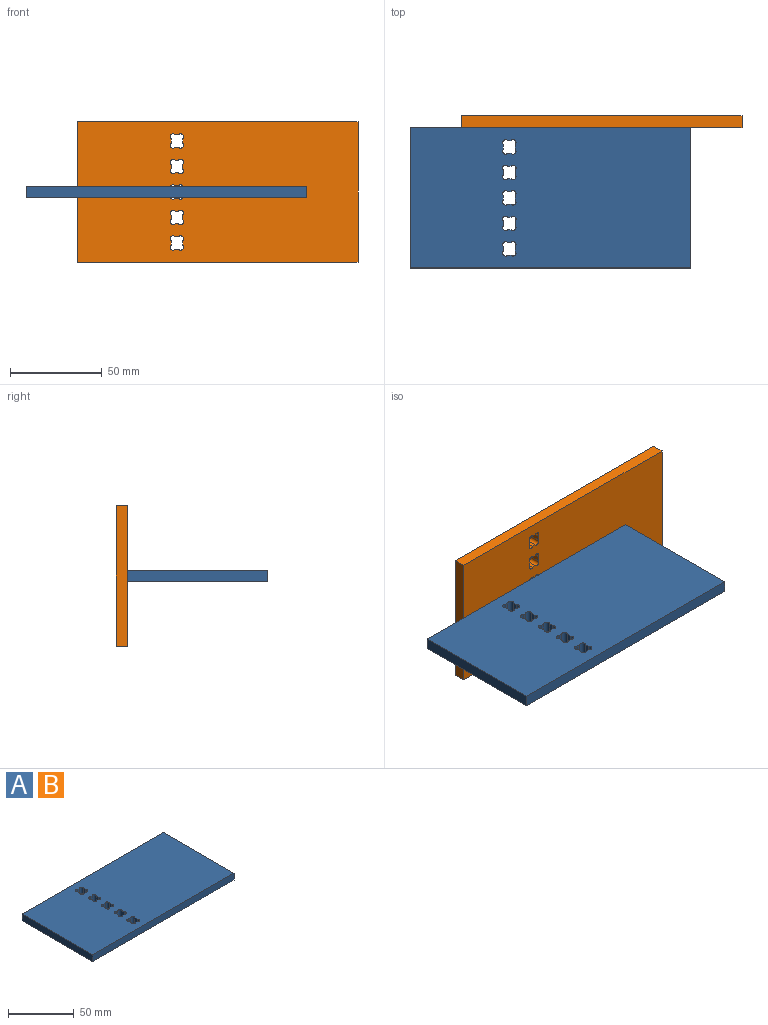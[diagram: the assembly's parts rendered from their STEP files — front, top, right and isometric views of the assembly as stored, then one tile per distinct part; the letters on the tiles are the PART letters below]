
ASSEMBLY  parts=2 mates=1
PART A: 46 faces, bbox 152.4x76.2x6.4 mm
  f0: plane 6.35x1.86mm, normal (0,-1,0), area 11.8mm2, adj f24,f25,f42,f45
  f1: plane 6.35x2.44mm, normal (-1,0,0), area 15.5mm2, adj f24,f25,f44,f45
  f2: plane 6.35x1.86mm, normal (0,1,0), area 11.8mm2, adj f24,f25,f43,f44
  f3: plane 6.35x2.44mm, normal (1,0,0), area 15.5mm2, adj f24,f25,f42,f43
  f4: plane 6.35x1.86mm, normal (0,-1,0), area 11.8mm2, adj f24,f25,f38,f41
  f5: plane 6.35x2.44mm, normal (-1,0,0), area 15.5mm2, adj f24,f25,f40,f41
  f6: plane 6.35x1.86mm, normal (0,1,0), area 11.8mm2, adj f24,f25,f39,f40
  f7: plane 6.35x2.44mm, normal (1,0,0), area 15.5mm2, adj f24,f25,f38,f39
  f8: plane 6.35x1.86mm, normal (0,-1,0), area 11.8mm2, adj f24,f25,f34,f37
  f9: plane 6.35x2.44mm, normal (-1,0,0), area 15.5mm2, adj f24,f25,f36,f37
  f10: plane 6.35x1.86mm, normal (0,1,0), area 11.8mm2, adj f24,f25,f35,f36
  f11: plane 6.35x2.44mm, normal (1,0,0), area 15.5mm2, adj f24,f25,f34,f35
  f12: plane 6.35x1.86mm, normal (0,-1,0), area 11.8mm2, adj f24,f25,f30,f33
  f13: plane 6.35x2.44mm, normal (-1,0,0), area 15.5mm2, adj f24,f25,f32,f33
  f14: plane 6.35x1.86mm, normal (0,1,0), area 11.8mm2, adj f24,f25,f31,f32
  f15: plane 6.35x2.44mm, normal (1,0,0), area 15.5mm2, adj f24,f25,f30,f31
  f16: plane 6.35x1.86mm, normal (0,-1,0), area 11.8mm2, adj f24,f25,f26,f29
  f17: plane 6.35x2.44mm, normal (-1,0,0), area 15.5mm2, adj f24,f25,f28,f29
  f18: plane 6.35x1.86mm, normal (0,1,0), area 11.8mm2, adj f24,f25,f27,f28
  f19: plane 6.35x2.44mm, normal (1,0,0), area 15.5mm2, adj f24,f25,f26,f27
  f20: plane 152.4x6.35mm, normal (0,1,0), area 967.7mm2, adj f21,f23,f24,f25
  f21: plane 76.2x6.35mm, normal (-1,0,0), area 483.9mm2, adj f20,f22,f24,f25
  f22: plane 152.4x6.35mm, normal (0,-1,0), area 967.7mm2, adj f21,f23,f24,f25
  f23: plane 76.2x6.35mm, normal (1,0,0), area 483.9mm2, adj f20,f22,f24,f25
  f24: plane 152.4x76.2mm, normal (0,0,1), area 11364.2mm2, adj f0,f1,f2,f3,f4,f5,f6,f7
  f25: plane 152.4x76.2mm, normal (0,0,-1), area 11364.2mm2, adj f0,f1,f2,f3,f4,f5,f6,f7
  f26: cylinder r=1.59mm len=6.35mm, axis (0,0,1), area 31.7mm2, adj f16,f19,f24,f25
  f27: cylinder r=1.59mm len=6.35mm, axis (0,0,1), area 31.7mm2, adj f18,f19,f24,f25
  f28: cylinder r=1.59mm len=6.35mm, axis (0,0,1), area 31.7mm2, adj f17,f18,f24,f25
  f29: cylinder r=1.59mm len=6.35mm, axis (0,0,1), area 31.7mm2, adj f16,f17,f24,f25
  f30: cylinder r=1.59mm len=6.35mm, axis (0,0,1), area 31.7mm2, adj f12,f15,f24,f25
  f31: cylinder r=1.59mm len=6.35mm, axis (0,0,1), area 31.7mm2, adj f14,f15,f24,f25
  f32: cylinder r=1.59mm len=6.35mm, axis (0,0,1), area 31.7mm2, adj f13,f14,f24,f25
  f33: cylinder r=1.59mm len=6.35mm, axis (0,0,1), area 31.7mm2, adj f12,f13,f24,f25
  f34: cylinder r=1.59mm len=6.35mm, axis (0,0,1), area 31.7mm2, adj f8,f11,f24,f25
  f35: cylinder r=1.59mm len=6.35mm, axis (0,0,1), area 31.7mm2, adj f10,f11,f24,f25
  f36: cylinder r=1.59mm len=6.35mm, axis (0,0,1), area 31.7mm2, adj f9,f10,f24,f25
  f37: cylinder r=1.59mm len=6.35mm, axis (0,0,1), area 31.7mm2, adj f8,f9,f24,f25
  f38: cylinder r=1.59mm len=6.35mm, axis (0,0,1), area 31.7mm2, adj f4,f7,f24,f25
  f39: cylinder r=1.59mm len=6.35mm, axis (0,0,1), area 31.7mm2, adj f6,f7,f24,f25
  f40: cylinder r=1.59mm len=6.35mm, axis (0,0,1), area 31.7mm2, adj f5,f6,f24,f25
  f41: cylinder r=1.59mm len=6.35mm, axis (0,0,1), area 31.7mm2, adj f4,f5,f24,f25
  f42: cylinder r=1.59mm len=6.35mm, axis (0,0,1), area 31.7mm2, adj f0,f3,f24,f25
  f43: cylinder r=1.59mm len=6.35mm, axis (0,0,1), area 31.7mm2, adj f2,f3,f24,f25
  f44: cylinder r=1.59mm len=6.35mm, axis (0,0,1), area 31.7mm2, adj f1,f2,f24,f25
  f45: cylinder r=1.59mm len=6.35mm, axis (0,0,1), area 31.7mm2, adj f0,f1,f24,f25
PART B: same geometry as A
PLACE A t=(-53.64,9.55,1.44)mm
PLACE B rot(axis=(1,0,0),90deg) t=(-25.6,92.1,-33.49)mm
MATE planar B.f24 <-> A.f20  axis (0,-1,0) through (51.08,85.75,4.61)mm
